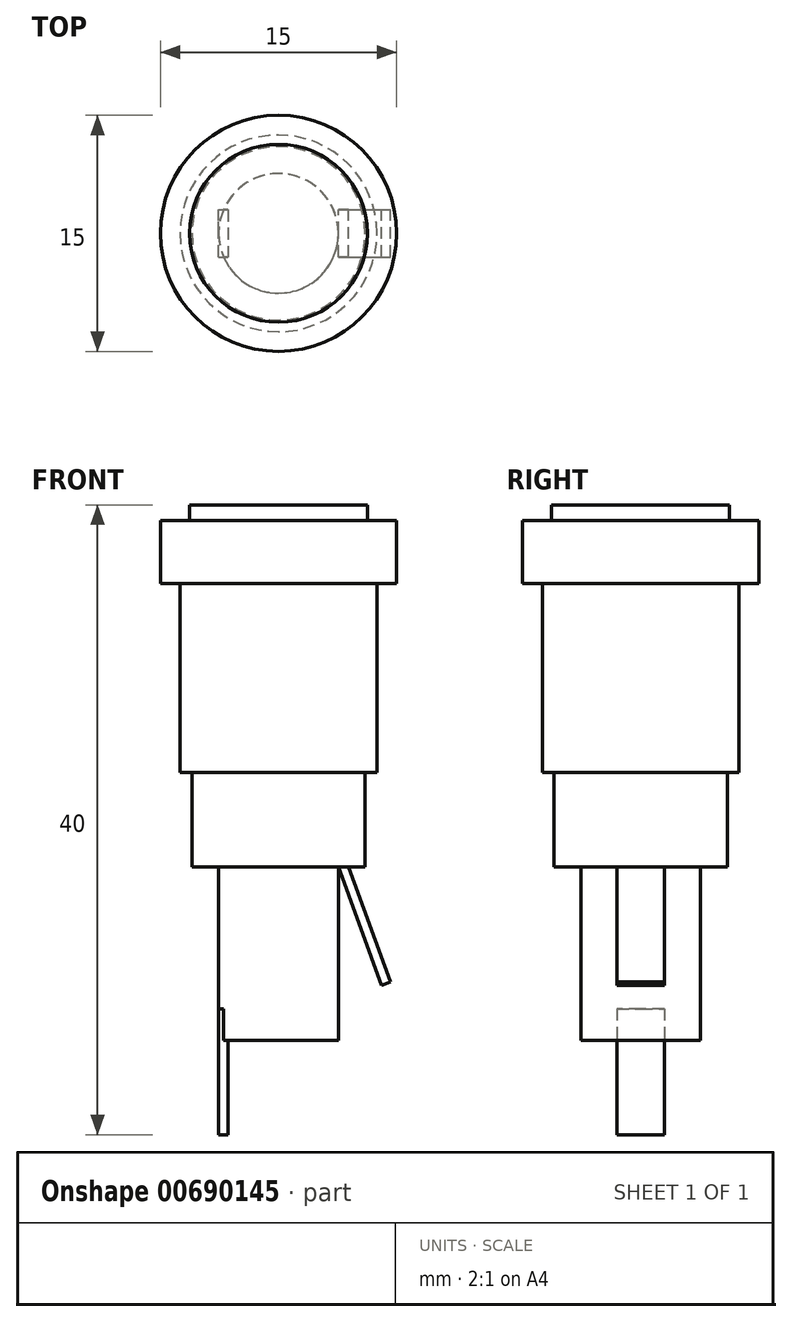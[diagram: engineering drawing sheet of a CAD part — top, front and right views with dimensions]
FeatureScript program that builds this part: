
annotation { "Feature Type Name" : "Feature", "Feature Type Description" : "" }
export const myFeature = defineFeature(function(context is Context, id is Id, definition is map)
    precondition{}
    {
        {
            var Q0;
            Q0=qCreatedBy(makeId("Front.planeOp"),FACE);
            var sketch = newSketch(context, id + "F0", { "sketchPlane" : qUnion([Q0])});
            skLineSegment(sketch, "E0", {"start": v(-5.65, 5) * mm, "end": v(5.65, 5) * mm});
            skLineSegment(sketch, "E1", {"start": v(5.65, 5) * mm, "end": v(5.65, 4) * mm});
            skLineSegment(sketch, "E2", {"start": v(5.65, 4) * mm, "end": v(7.5, 4) * mm});
            skLineSegment(sketch, "E3", {"start": v(7.5, 4) * mm, "end": v(7.5, 0) * mm});
            skLineSegment(sketch, "E4", {"start": v(7.5, 0) * mm, "end": v(6.25, 0) * mm});
            skLineSegment(sketch, "E5", {"start": v(6.25, 0) * mm, "end": v(6.25, -12) * mm});
            skLineSegment(sketch, "E6", {"start": v(6.25, -12) * mm, "end": v(5.5, -12) * mm});
            skLineSegment(sketch, "E7", {"start": v(5.5, -12) * mm, "end": v(5.5, -18) * mm});
            skLineSegment(sketch, "E8", {"start": v(5.5, -18) * mm, "end": v(3.8, -18) * mm});
            skLineSegment(sketch, "E9", {"start": v(3.8, -18) * mm, "end": v(3.8, -29) * mm});
            skLineSegment(sketch, "E10", {"start": v(3.8, -29) * mm, "end": v(-3.8, -29) * mm});
            skLineSegment(sketch, "E11", {"start": v(0, -29) * mm, "end": v(0, 5) * mm});
            skLineSegment(sketch, "E12.MirrorCS", {"start": v(-5.65, 4) * mm, "end": v(-7.5, 4) * mm});
            skLineSegment(sketch, "E13.MirrorCS", {"start": v(-7.5, 0) * mm, "end": v(-6.25, 0) * mm});
            skLineSegment(sketch, "E14.MirrorCS", {"start": v(-5.5, -18) * mm, "end": v(-3.8, -18) * mm});
            skLineSegment(sketch, "E15.MirrorCS", {"start": v(-6.25, -12) * mm, "end": v(-5.5, -12) * mm});
            skLineSegment(sketch, "E16.MirrorCS", {"start": v(-5.65, 5) * mm, "end": v(-5.65, 4) * mm});
            skLineSegment(sketch, "E17.MirrorCS", {"start": v(-7.5, 4) * mm, "end": v(-7.5, 0) * mm});
            skLineSegment(sketch, "E18.MirrorCS", {"start": v(-3.8, -18) * mm, "end": v(-3.8, -29) * mm});
            skLineSegment(sketch, "E19.MirrorCS", {"start": v(-5.5, -12) * mm, "end": v(-5.5, -18) * mm});
            skLineSegment(sketch, "E20.MirrorCS", {"start": v(-6.25, 0) * mm, "end": v(-6.25, -12) * mm});
            skLineSegment(sketch, "E21.bottom", {"start": v(-3.8, -27) * mm, "end": v(-3.2, -27) * mm});
            skLineSegment(sketch, "E21.top", {"start": v(-3.8, -35) * mm, "end": v(-3.2, -35) * mm});
            skLineSegment(sketch, "E21.left", {"start": v(-3.8, -27) * mm, "end": v(-3.8, -35) * mm});
            skLineSegment(sketch, "E21.right", {"start": v(-3.2, -27) * mm, "end": v(-3.2, -35) * mm});
            skLineSegment(sketch, "E22.bottom", {"start": v(3.8, -18) * mm, "end": v(4.36, -17.8) * mm});
            skLineSegment(sketch, "E22.top", {"start": v(6.54, -25.52) * mm, "end": v(7.1, -25.31) * mm});
            skLineSegment(sketch, "E22.left", {"start": v(3.8, -18) * mm, "end": v(6.54, -25.52) * mm});
            skLineSegment(sketch, "E22.right", {"start": v(4.36, -17.8) * mm, "end": v(7.1, -25.31) * mm});
            skSolve(sketch);
        }
        {
            var Q0;
            {var subQ1=sQuery(id+"F0.wireOp",EDGE,"E11");Q0=makeQuery(id+"F0.imprint","IMPRINT",FACE,{"disambiguationData":[TD([[makeQuery(id+"F0.imprint","IMPRINT",EDGE,{"derivedFrom":subQ1}),1.0]])]});}
            var Q1;
            {var subQ5=sQuery(id+"F0.wireOp",EDGE,"E21.bottom");Q1=makeQuery(id+"F0.imprint","IMPRINT",FACE,{"disambiguationData":[TD([[makeQuery(id+"F0.imprint","IMPRINT",EDGE,{"derivedFrom":subQ5}),-1.0]])]});}
            var Q2;
            Q2=sQuery(id+"F0.wireOp",EDGE,"E11");
            revolve(context, id + "F1", {"surfaceOperationType" : NewSurfaceOperationType.NEW, "entities" : qUnion([Q0, Q1]), "axis" : qUnion([Q2]), "revolveType" : RevolveType.FULL});
        }
        {
            var Q0;
            Q0=makeQuery(id+"F0.imprint","IMPRINT",FACE,{"disambiguationData":[TD([[makeQuery(id+"F0.imprint","IMPRINT",EDGE,{"derivedFrom":sQuery(id+"F0.wireOp",EDGE,"E21.top")}),1.0]])]});
            var Q1;
            {var subQ4=sQuery(id+"F0.wireOp",EDGE,"E22.top");Q1=makeQuery(id+"F0.imprint","IMPRINT",FACE,{"disambiguationData":[TD([[makeQuery(id+"F0.imprint","IMPRINT",EDGE,{"derivedFrom":subQ4}),1.0]])]});}
            var Q2;
            {var subQ5=sQuery(id+"F0.wireOp",EDGE,"E21.bottom");Q2=makeQuery(id+"F0.imprint","IMPRINT",FACE,{"disambiguationData":[TD([[makeQuery(id+"F0.imprint","IMPRINT",EDGE,{"derivedFrom":subQ5}),-1.0]])]});}
            extrude(context, id + "F2", {"entities" : qUnion([Q0, Q1, Q2]), "operationType" : NewBodyOperationType.ADD, "endBound" : BoundingType.SYMMETRIC, "depth" : 3 * mm, "offsetDistance" : 25 * mm});
        }
    });
